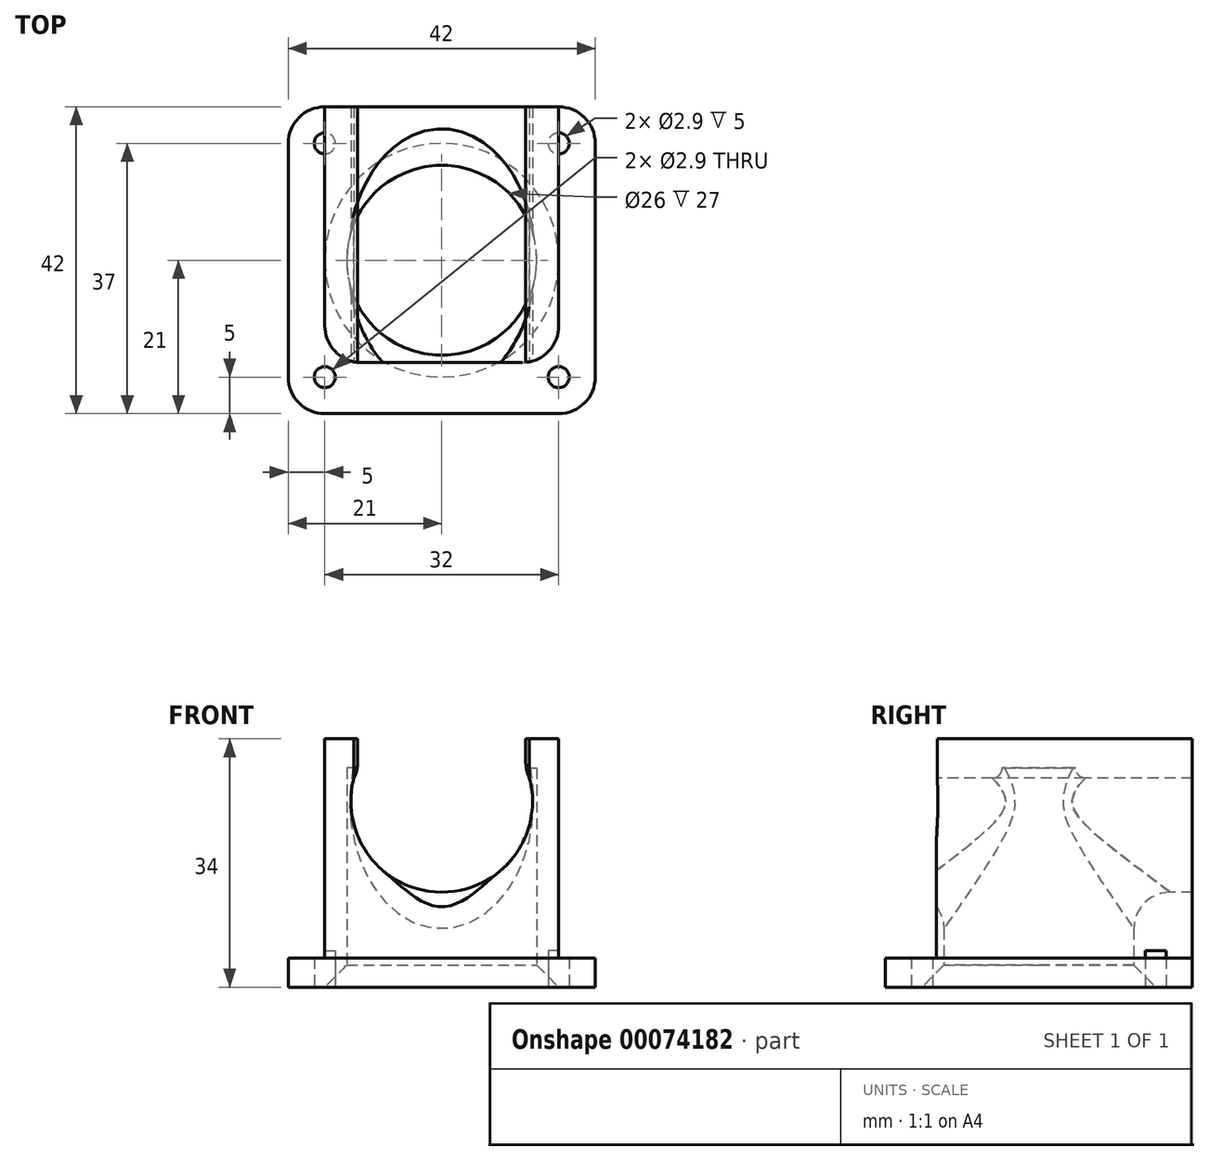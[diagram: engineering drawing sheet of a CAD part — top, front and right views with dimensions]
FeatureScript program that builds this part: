
annotation { "Feature Type Name" : "Feature", "Feature Type Description" : "" }
export const myFeature = defineFeature(function(context is Context, id is Id, definition is map)
    precondition{}
    {
        {
            var Q0;
            Q0=qCreatedBy(makeId("Top.planeOp"),FACE);
            var sketch = newSketch(context, id + "F0", { "sketchPlane" : qUnion([Q0])});
            skLineSegment(sketch, "E0.bottom", {"start": v(0, 0) * mm, "end": v(42, 0) * mm});
            skLineSegment(sketch, "E0.top", {"start": v(0, 42) * mm, "end": v(42, 42) * mm});
            skLineSegment(sketch, "E0.left", {"start": v(0, 0) * mm, "end": v(0, 42) * mm});
            skLineSegment(sketch, "E0.right", {"start": v(42, 0) * mm, "end": v(42, 42) * mm});
            skSolve(sketch);
        }
        {
            var Q0;
            Q0=qSketchRegion(id+"F0",true);
            extrude(context, id + "F1", {"entities" : qUnion([Q0]), "depth" : 4 * mm});
        }
        {
            var Q0;
            Q0=makeQuery(id+"F1.opExtrude","CAP_FACE",FACE,{"disambiguationData":[OSD([sQuery(id+"F0.wireOp",EDGE,"E0.bottom"),sQuery(id+"F0.wireOp",EDGE,"E0.top"),sQuery(id+"F0.wireOp",EDGE,"E0.left"),sQuery(id+"F0.wireOp",EDGE,"E0.right")])],"isStart":false});
            var sketch = newSketch(context, id + "F2", { "sketchPlane" : qUnion([Q0])});
            skLineSegment(sketch, "E1.bottom", {"start": v(5, 42) * mm, "end": v(37, 42) * mm});
            skLineSegment(sketch, "E1.top", {"start": v(5, 7) * mm, "end": v(37, 7) * mm});
            skLineSegment(sketch, "E1.left", {"start": v(5, 42) * mm, "end": v(5, 7) * mm});
            skLineSegment(sketch, "E1.right", {"start": v(37, 42) * mm, "end": v(37, 7) * mm});
            skLineSegment(sketch, "E2", {"start": v(37, 21) * mm, "end": v(42, 21) * mm});
            skLineSegment(sketch, "E3", {"start": v(5, 19.4) * mm, "end": v(0, 19.4) * mm});
            skSolve(sketch);
        }
        {
            var Q0;
            Q0=qSketchRegion(id+"F2",true);
            extrude(context, id + "F3", {"entities" : qUnion([Q0]), "operationType" : NewBodyOperationType.ADD, "depth" : 30 * mm});
        }
        {
            var Q0;
            Q0=makeQuery(id+"F1.opExtrude","CAP_FACE",FACE,{"disambiguationData":[OSD([sQuery(id+"F0.wireOp",EDGE,"E0.bottom"),sQuery(id+"F0.wireOp",EDGE,"E0.top"),sQuery(id+"F0.wireOp",EDGE,"E0.left"),sQuery(id+"F0.wireOp",EDGE,"E0.right")])],"isStart":true});
            var sketch = newSketch(context, id + "F4", { "sketchPlane" : qUnion([Q0])});
            skCircle(sketch, "E4", {"center": v(21, -21) * mm, "radius": 19 * mm});
            skLineSegment(sketch, "E5", {"start": v(21, -21) * mm, "end": v(21, 0) * mm});
            skLineSegment(sketch, "E6", {"start": v(21, -21) * mm, "end": v(42, -21) * mm});
            skSolve(sketch);
        }
        {
            var Q0;
            Q0=qSketchRegion(id+"F4",true);
            extrude(context, id + "F5", {"entities" : qUnion([Q0]), "operationType" : NewBodyOperationType.REMOVE, "oppositeDirection" : true, "depth" : 3 * mm});
        }
        {
            var Q0;
            Q0=makeQuery(id+"F5.boolean.opBoolean","COPY",FACE,{"derivedFrom":makeQuery(id+"F5.opExtrude","CAP_FACE",FACE,{"disambiguationData":[OSD([sQuery(id+"F4.wireOp",EDGE,"E4")])],"isStart":false})});
            var sketch = newSketch(context, id + "F6", { "sketchPlane" : qUnion([Q0])});
            skCircle(sketch, "E7", {"center": v(21, -21) * mm, "radius": 13 * mm});
            skSolve(sketch);
        }
        {
            var Q0;
            Q0=qSketchRegion(id+"F6",true);
            extrude(context, id + "F7", {"entities" : qUnion([Q0]), "operationType" : NewBodyOperationType.REMOVE, "oppositeDirection" : true, "depth" : 27 * mm});
        }
        {
            var Q0;
            Q0=makeQuery(id+"F3.opExtrude","SWEPT_FACE",FACE,{"disambiguationData":[OSD([sQuery(id+"F2.wireOp",EDGE,"E1.top")])]});
            var sketch = newSketch(context, id + "F8", { "sketchPlane" : qUnion([Q0])});
            skLineSegment(sketch, "E8", {"start": v(9, 34) * mm, "end": v(9, 28.62) * mm});
            skLineSegment(sketch, "E9", {"start": v(33, 34) * mm, "end": v(33, 28.62) * mm});
            skLineSegment(sketch, "E10", {"start": v(9, 28.62) * mm, "end": v(5, 28.62) * mm, "construction": true});
            skLineSegment(sketch, "E11", {"start": v(33, 28.62) * mm, "end": v(37, 28.62) * mm, "construction": true});
            skCircle(sketch, "E12", {"center": v(21, 25.42) * mm, "radius": 12.42 * mm});
            skSolve(sketch);
        }
        {
            var Q0;
            Q0=qSketchRegion(id+"F8",true);
            var Q1;
            {var subQ3=sQuery(id+"F8.wireOp",EDGE,"E8");Q1=makeQuery(id+"F8.imprint","IMPRINT",FACE,{"disambiguationData":[TD([[makeQuery(id+"F8.imprint","IMPRINT",EDGE,{"derivedFrom":subQ3}),1.0]])]});}
            var Q2;
            {var subQ3=sQuery(id+"F8.wireOp",EDGE,"E9");Q2=makeQuery(id+"F8.imprint","IMPRINT",FACE,{"disambiguationData":[TD([[makeQuery(id+"F8.imprint","IMPRINT",EDGE,{"derivedFrom":subQ3}),-1.0]])]});}
            extrude(context, id + "F9", {"entities" : qUnion([Q0, Q1, Q2]), "operationType" : NewBodyOperationType.REMOVE, "endBound" : BoundingType.THROUGH_ALL, "oppositeDirection" : true, "depth" : 25 * mm});
        }
        {
            var Q0;
            Q0=makeQuery(id+"F1.opExtrude","SWEPT_EDGE",EDGE,{"disambiguationData":[OSD([sQuery(id+"F0.wireOp",EDGE,"E0.top"),sQuery(id+"F0.wireOp",EDGE,"E0.right")])]});
            var Q1;
            Q1=makeQuery(id+"F1.opExtrude","SWEPT_EDGE",EDGE,{"disambiguationData":[OSD([sQuery(id+"F0.wireOp",EDGE,"E0.top"),sQuery(id+"F0.wireOp",EDGE,"E0.left")])]});
            var Q2;
            Q2=makeQuery(id+"F1.opExtrude","SWEPT_EDGE",EDGE,{"disambiguationData":[OSD([sQuery(id+"F0.wireOp",EDGE,"E0.bottom"),sQuery(id+"F0.wireOp",EDGE,"E0.left")])]});
            var Q3;
            Q3=makeQuery(id+"F1.opExtrude","SWEPT_EDGE",EDGE,{"disambiguationData":[OSD([sQuery(id+"F0.wireOp",EDGE,"E0.bottom"),sQuery(id+"F0.wireOp",EDGE,"E0.right")])]});
            fillet(context, id + "F10", {"entities" : qUnion([Q0, Q1, Q2, Q3]), "radius" : 5 * mm, "tangentPropagation" : true, "allowEdgeOverflow" : false});
        }
        {
            var Q0;
            Q0=makeQuery(id+"F3.opExtrude","SWEPT_EDGE",EDGE,{"disambiguationData":[OSD([sQuery(id+"F2.wireOp",EDGE,"E1.top"),sQuery(id+"F2.wireOp",EDGE,"E1.left")])]});
            var Q1;
            Q1=makeQuery(id+"F3.opExtrude","SWEPT_EDGE",EDGE,{"disambiguationData":[OSD([sQuery(id+"F2.wireOp",EDGE,"E1.top"),sQuery(id+"F2.wireOp",EDGE,"E1.right")])]});
            var Q2;
            Q2=makeQuery(id+"F10.opFillet","BLEND_EDGE",EDGE,{"blendedFrom":[makeQuery(id+"F1.opExtrude","SWEPT_EDGE",EDGE,{"disambiguationData":[OSD([sQuery(id+"F0.wireOp",EDGE,"E0.bottom"),sQuery(id+"F0.wireOp",EDGE,"E0.right")])]}),makeQuery(id+"F3.opExtrude","SWEPT_FACE",FACE,{"disambiguationData":[OSD([sQuery(id+"F2.wireOp",EDGE,"E1.right")])]})],"blendedInto":[makeQuery(id+"F3.opExtrude","SWEPT_FACE",FACE,{"disambiguationData":[OSD([sQuery(id+"F2.wireOp",EDGE,"E1.right")])]})]});
            fillet(context, id + "F11", {"entities" : qUnion([Q0, Q1, Q2]), "radius" : 5 * mm, "tangentPropagation" : true, "allowEdgeOverflow" : false});
        }
        {
            var Q0;
            {var subQ0=sQuery(id+"F8.wireOp",EDGE,"E12");Q0=makeQuery(id+"F9.boolean.opBoolean","INTERSECT",EDGE,{"derivedFrom":[makeQuery(id+"F7.boolean.opBoolean","COPY",FACE,{"derivedFrom":makeQuery(id+"F7.opExtrude","SWEPT_FACE",FACE,{"disambiguationData":[OSD([sQuery(id+"F6.wireOp",EDGE,"E7")])]})}),makeQuery(id+"F9.opExtrude","SWEPT_FACE",FACE,{"disambiguationData":[OSD([subQ0]),TDD([makeQuery(id+"F8.imprint","IMPRINT",EDGE,{"disambiguationData":[TD([[makeQuery(id+"F8.imprint","INTERSECT",VERTEX,{"derivedFrom":[sQuery(id+"F8.wireOp",EDGE,"E8"),subQ0]}),-1.0]])],"derivedFrom":subQ0})])]})]});}
            fillet(context, id + "F12", {"entities" : qUnion([Q0]), "radius" : 5 * mm, "tangentPropagation" : true, "allowEdgeOverflow" : false});
        }
        {
            var Q0;
            Q0=makeQuery(id+"F1.opExtrude","CAP_FACE",FACE,{"disambiguationData":[OSD([sQuery(id+"F0.wireOp",EDGE,"E0.bottom"),sQuery(id+"F0.wireOp",EDGE,"E0.top"),sQuery(id+"F0.wireOp",EDGE,"E0.left"),sQuery(id+"F0.wireOp",EDGE,"E0.right")])],"isStart":true});
            var sketch = newSketch(context, id + "F13", { "sketchPlane" : qUnion([Q0])});
            skCircle(sketch, "E13", {"center": v(5, -5) * mm, "radius": 1.45 * mm});
            skCircle(sketch, "E14", {"center": v(37, -5) * mm, "radius": 1.45 * mm});
            skCircle(sketch, "E15", {"center": v(37, -37) * mm, "radius": 1.45 * mm});
            skCircle(sketch, "E16", {"center": v(5, -37) * mm, "radius": 1.45 * mm});
            skSolve(sketch);
        }
        {
            var Q0;
            Q0=qSketchRegion(id+"F13",true);
            extrude(context, id + "F14", {"entities" : qUnion([Q0]), "operationType" : NewBodyOperationType.REMOVE, "oppositeDirection" : true, "depth" : 5 * mm});
        }
        {
            var Q0;
            Q0=makeQuery(id+"F5.boolean.opBoolean","COPY",EDGE,{"derivedFrom":makeQuery(id+"F5.opExtrude","CAP_EDGE",EDGE,{"disambiguationData":[OSD([sQuery(id+"F4.wireOp",EDGE,"E4")])],"isStart":false})});
            chamfer(context, id + "F15", {"entities" : qUnion([Q0]), "width" : 6 * mm, "tangentPropagation" : true});
        }
        {
            var Q0;
            Q0=makeQuery(id+"F9.boolean.opBoolean","COPY",FACE,{"derivedFrom":makeQuery(id+"F9.opExtrude","SWEPT_FACE",FACE,{"disambiguationData":[OSD([sQuery(id+"F8.wireOp",EDGE,"E8")])]})});
            var sketch = newSketch(context, id + "F16", { "sketchPlane" : qUnion([Q0])});
            skLineSegment(sketch, "E17.bottom", {"start": v(7.1, 34) * mm, "end": v(42, 34) * mm});
            skLineSegment(sketch, "E17.top", {"start": v(7.1, 28.62) * mm, "end": v(42, 28.62) * mm});
            skLineSegment(sketch, "E17.left", {"start": v(7.1, 34) * mm, "end": v(7.1, 28.62) * mm});
            skLineSegment(sketch, "E17.right", {"start": v(42, 34) * mm, "end": v(42, 28.62) * mm});
            skSolve(sketch);
        }
        {
            var Q0;
            Q0=qSketchRegion(id+"F16",true);
            extrude(context, id + "F17", {"entities" : qUnion([Q0]), "operationType" : NewBodyOperationType.ADD, "depth" : 0.5 * mm});
        }
        {
            var Q0;
            Q0=makeQuery(id+"F9.boolean.opBoolean","COPY",FACE,{"derivedFrom":makeQuery(id+"F9.opExtrude","SWEPT_FACE",FACE,{"disambiguationData":[OSD([sQuery(id+"F8.wireOp",EDGE,"E9")])]})});
            var sketch = newSketch(context, id + "F18", { "sketchPlane" : qUnion([Q0])});
            skLineSegment(sketch, "E18.bottom", {"start": v(-42, 34) * mm, "end": v(-7.1, 34) * mm});
            skLineSegment(sketch, "E18.top", {"start": v(-42, 28.62) * mm, "end": v(-7.1, 28.62) * mm});
            skLineSegment(sketch, "E18.left", {"start": v(-42, 34) * mm, "end": v(-42, 28.62) * mm});
            skLineSegment(sketch, "E18.right", {"start": v(-7.1, 34) * mm, "end": v(-7.1, 28.62) * mm});
            skSolve(sketch);
        }
        {
            var Q0;
            Q0=qSketchRegion(id+"F18",true);
            extrude(context, id + "F19", {"entities" : qUnion([Q0]), "operationType" : NewBodyOperationType.ADD, "depth" : 0.5 * mm});
        }
        {
            var Q0;
            Q0=makeQuery(id+"F19.opExtrude","CAP_EDGE",EDGE,{"disambiguationData":[OSD([sQuery(id+"F18.wireOp",EDGE,"E18.top")])],"isStart":false});
            var Q1;
            Q1=makeQuery(id+"F17.opExtrude","CAP_EDGE",EDGE,{"disambiguationData":[OSD([sQuery(id+"F16.wireOp",EDGE,"E17.top")])],"isStart":false});
            fillet(context, id + "F20", {"entities" : qUnion([Q0, Q1]), "radius" : 5 * mm, "tangentPropagation" : true, "allowEdgeOverflow" : false});
        }
    });
